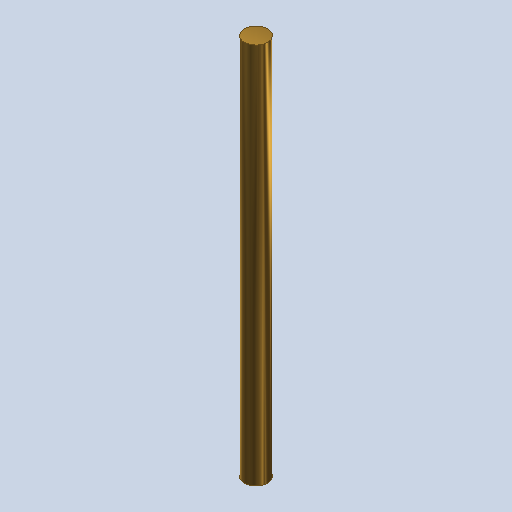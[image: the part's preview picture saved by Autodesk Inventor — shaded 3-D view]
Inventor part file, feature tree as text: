
AUTODESK INVENTOR PART (.ipt)
format: ipt  version: 2023 (Build 270158030, 158C)  size: 107,520 bytes
history: native  units: mm
features: other x1, extrude x1, sketch x1
ambient origin geometry x8: Origin, YZ Plane, XZ Plane, XY Plane, X Axis, Y Axis, Z Axis, Center Point
bodies: Body1 (feature_tree)
feature tree (3):
  other  "ソリッド1"
  extrude  "押し出し1"  Depth=3.0mm
  sketch  "スケッチ1"
